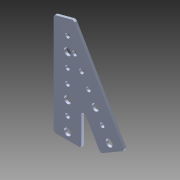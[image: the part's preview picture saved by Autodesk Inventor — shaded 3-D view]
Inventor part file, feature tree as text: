
AUTODESK INVENTOR PART (.ipt)
format: ipt  version: 2015 SP1 (Build 190203100, 203)  size: 172,544 bytes
history: native  units: in
note: dims shown in document units (in); Inventor stores cm internally (conversion verified against a paired STEP export)
features: other x2, extrude x2, sketch x2, imported_body x1, projected_geometry x1
ambient origin geometry x8: Origin, YZ Plane, XZ Plane, XY Plane, X Axis, Y Axis, Z Axis, Center Point
bodies: Body1 (feature_tree)
feature tree (8):
  other  "Cut-Extrude2"
  other  "Versaframe 30deg gusset1"
  extrude  "Extrusion1"  Depth=0.25in
  extrude  "Extrusion2"  Depth=1.0in
  imported_body  "Base1"
  sketch  "Sketch1"  dims[d0=0.25in d1=0.25in]
  projected_geometry  "Projected Loop1"
  sketch  "Sketch2"  dims[d2=1.0in d3=0.0in d4=0.25in d5=0.25in d6=0.25in d7=1.0in d8=0.0in]
